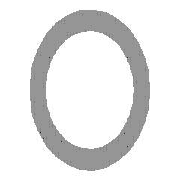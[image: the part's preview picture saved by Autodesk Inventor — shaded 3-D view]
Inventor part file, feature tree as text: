
AUTODESK INVENTOR PART (.ipt)
format: ipt  version: 2021 (Build 250183000, 183)  size: 758,784 bytes
history: native  units: mm (DEFAULTED — no unit token found)
features: other x16, plane x5, sketch x3, sweep x1, split x1
ambient origin geometry x8: Origin, YZ Plane, XZ Plane, XY Plane, X Axis, Y Axis, Z Axis, Center Point
bodies: Solid1 (feature_tree)
feature tree (26):
  parser-record x2  (decoder bookkeeping rows leaked as tree rows — omitted from the tree; the rows remain in map.json)
  other  "Driven Length"
  other  "Plano inicial"
  other  "Plano final"
  other  "Trayectoria de barrido"
  plane  "Plano de trabajo de orientación"
  sweep  "Cuerpo"
  plane  "Plano de trabajo7"
  split  "Dividir3"
  plane  "Plano de trabajo8"
  plane  "Plano de trabajo9"
  sketch  "Sketch3"  dims[d0=26.67mm d1=2.8702mm]
  plane  "Work Plane3"
  sketch  "Sketch4"  dims[d4=-0.0mm]
  sketch  "Boceto7"  dims[d5=1154.403192mm d6=90.0deg d7=1154.403192mm d8=0.0mm d9=0.0mm d38=16.002mm d39=254.157378mm d64=0.0mm d65=90.0deg d66=0.0mm d67=90.0deg d108=5.0mm d109=0.0mm d110=5.0mm d111=0.0mm]
  other  "Sup36"
  other  "Sup68"
  other  "Sup69"
  other  "Sólido23"
  other  "SuperficieSolevación3"
  other  "Sup67"
  other  "Superficie de contorno43"
  other  "Superficie de contorno44"
  other  "Marco_Bicicleta.iam"
  other  "Esqueleto_estructura:1"
note: 1 file-system path scrubbed to <path> (originals preserved in map.json)
